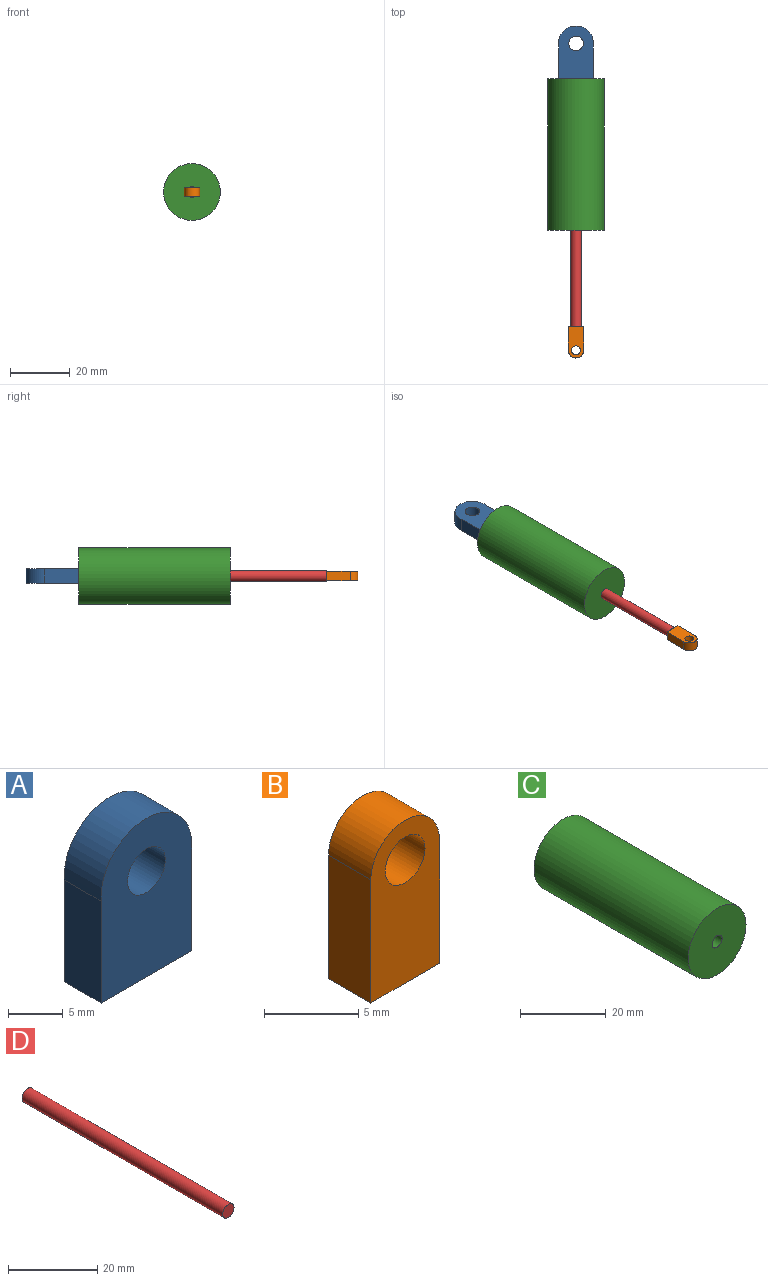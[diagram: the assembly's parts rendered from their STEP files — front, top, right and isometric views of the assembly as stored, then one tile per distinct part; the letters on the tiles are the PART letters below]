
ASSEMBLY  parts=4 mates=3
PART A: 7 faces, bbox 11.7x4.8x17.7 mm
  f0: cylinder r=5.86mm len=11.73mm, axis (0,1,0), area 92.2mm2, adj f1,f3,f5,f6
  f1: plane 11.39x4.75mm, normal (-1,0,0), area 54.1mm2, adj f0,f2,f5,f6
  f2: plane 11.68x4.75mm, normal (0,0,-1), area 55.5mm2, adj f1,f3,f5,f6
  f3: plane 11.39x4.75mm, normal (1,0,0), area 54.1mm2, adj f0,f2,f5,f6
  f4: cylinder r=2.45mm len=4.89mm, axis (0,1,0), area 73mm2, adj f5,f6
  f5: plane 17.75x11.73mm, normal (0,-1,0), area 174.1mm2, adj f0,f1,f2,f3,f4
  f6: plane 17.75x11.73mm, normal (0,1,0), area 174.1mm2, adj f0,f1,f2,f3,f4
PART B: 9 faces, bbox 5.2x3.2x10.6 mm
  f0: plane 8.01x3.18mm, normal (1,0,0), area 25.4mm2, adj f1,f6,f7,f8
  f1: plane 3.18x0.01mm, normal (0,0,1), area 0mm2, adj f0,f2,f7,f8
  f2: cylinder r=2.58mm len=5.15mm, axis (0,1,0), area 25.7mm2, adj f1,f3,f7,f8
  f3: plane 3.18x0.01mm, normal (0,0,1), area 0mm2, adj f2,f4,f7,f8
  f4: plane 8.01x3.18mm, normal (-1,0,0), area 25.4mm2, adj f3,f6,f7,f8
  f5: cylinder r=1.49mm len=3.18mm, axis (0,1,0), area 29.7mm2, adj f7,f8
  f6: plane 5.17x3.18mm, normal (0,0,-1), area 16.4mm2, adj f0,f4,f7,f8
  f7: plane 10.59x5.17mm, normal (0,-1,0), area 44.8mm2, adj f0,f1,f2,f3,f4,f5,f6
  f8: plane 10.59x5.17mm, normal (0,1,0), area 44.8mm2, adj f0,f1,f2,f3,f4,f5,f6
PART C: 4 faces, bbox 19.1x50.8x19.1 mm
  f0: cylinder r=9.53mm len=50.8mm, axis (0,1,0), area 3040.2mm2, adj f1,f2
  f1: plane 19.05x19.05mm, normal (0,-1,0), area 276.5mm2, adj f0,f3
  f2: plane 19.05x19.05mm, normal (0,1,0), area 276.5mm2, adj f0,f3
  f3: cylinder r=1.65mm len=50.8mm, axis (0,-1,0), area 526.7mm2, adj f1,f2
PART D: 3 faces, bbox 3.6x63.5x3.6 mm
  f0: cylinder r=1.79mm len=63.5mm, axis (0,1,0), area 712.4mm2, adj f1,f2
  f1: plane 3.57x3.57mm, normal (0,-1,0), area 10mm2, adj f0
  f2: plane 3.57x3.57mm, normal (0,1,0), area 10mm2, adj f0
PLACE A rot(axis=(-1,0,0),90deg) t=(-92.74,-86.93,-58.42)mm
PLACE B rot(axis=(1,0,0),90deg) t=(-41.36,-131.3,-54.46)mm
PLACE C t=(-20.15,-66.53,-68.52)mm fixed
PLACE D t=(-22.63,-86.09,-103.11)mm
MATE fastened B.f6 <-> D.f0  axis (0,1,0) through (-62.14,-149.59,-56.05)mm
MATE fastened A.f2 <-> C.f0  axis (0,-1,0) through (-62.14,-66.53,-56.05)mm
MATE slider C.f0 <-> D.f0  axis (0,1,0) through (-62.14,-66.53,-56.05)mm
